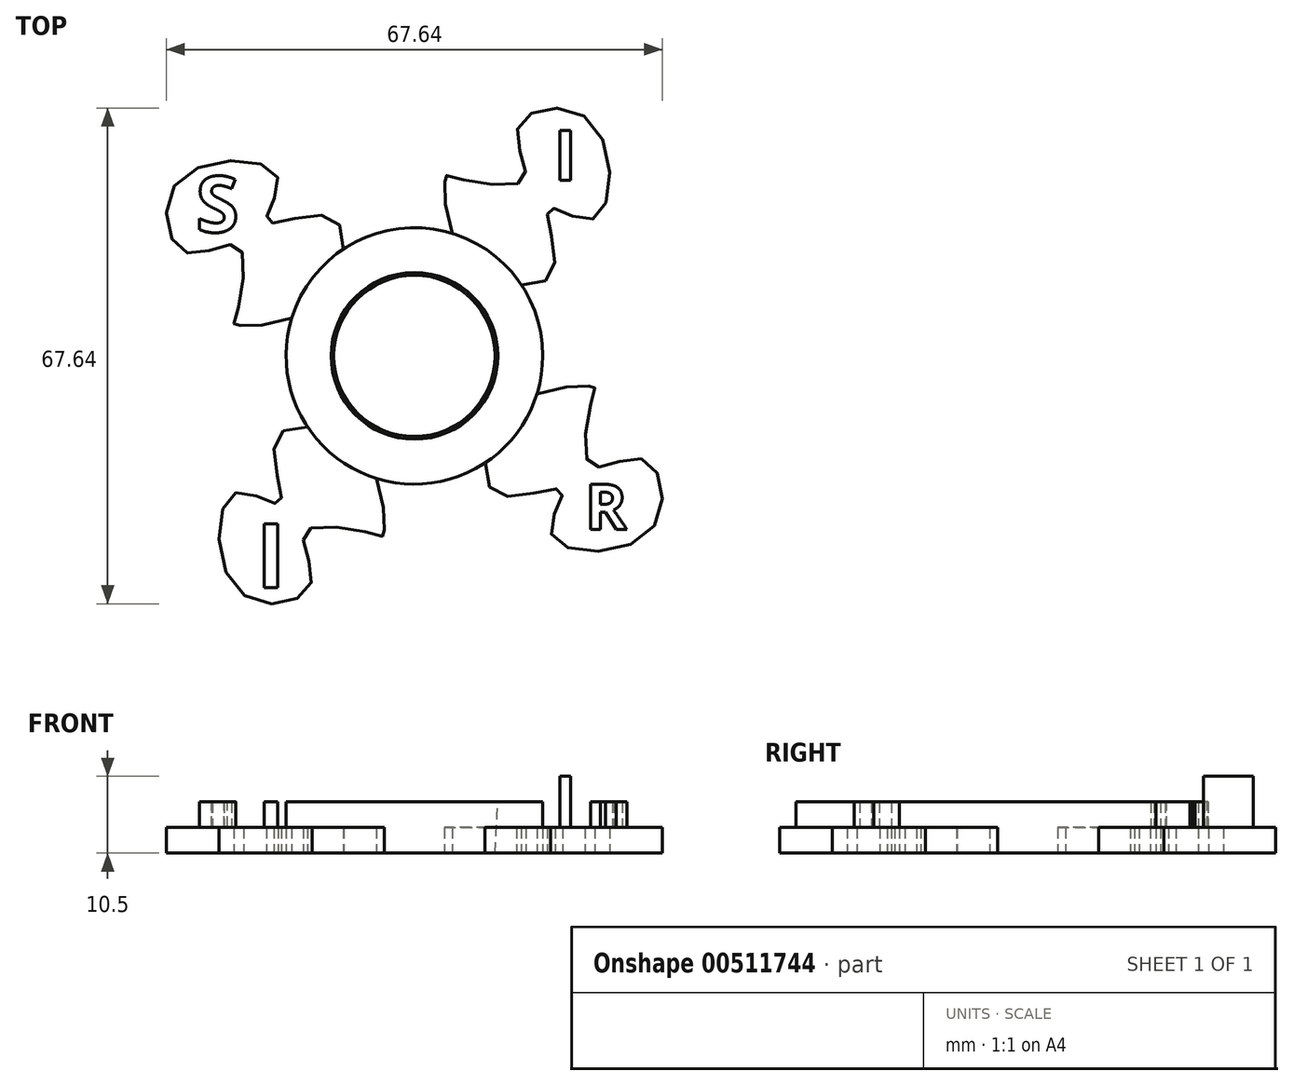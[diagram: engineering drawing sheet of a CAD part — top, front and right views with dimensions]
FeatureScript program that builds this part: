
annotation { "Feature Type Name" : "Feature", "Feature Type Description" : "" }
export const myFeature = defineFeature(function(context is Context, id is Id, definition is map)
    precondition{}
    {
        {
            var Q0;
            Q0=qCreatedBy(makeId("Top.planeOp"),FACE);
            var sketch = newSketch(context, id + "F0", { "sketchPlane" : qUnion([Q0])});
            skCircle(sketch, "E0", {"center": v(0, 0) * mm, "radius": 17.5 * mm});
            skSolve(sketch);
        }
        {
            var Q0;
            Q0 = qSketchRegion(id + "F0", true);
            extrude(context, id + "F1", {"entities" : qUnion([Q0]), "depth" : 7 * mm});
        }
        {
            var Q0;
            Q0=qCreatedBy(makeId("Top.planeOp"),FACE);
            var sketch = newSketch(context, id + "F2", { "sketchPlane" : qUnion([Q0])});
            skCircle(sketch, "E1", {"center": v(0, 0) * mm, "radius": 11 * mm});
            skSolve(sketch);
        }
        {
            var Q0;
            Q0=makeQuery(id+"F2.imprint","IMPRINT",FACE,{"disambiguationData":[TD([[makeQuery(id+"F2.imprint","IMPRINT",EDGE,{"derivedFrom":sQuery(id+"F2.wireOp",EDGE,"E1")}),1.0]])]});
            extrude(context, id + "F3", {"entities" : qUnion([Q0]), "operationType" : NewBodyOperationType.REMOVE, "depth" : 25 * mm, "hasDraft" : true, "draftAngle" : 3 * degree});
        }
        {
            var Q0;
            Q0=qCreatedBy(makeId("Top.planeOp"),FACE);
            var sketch = newSketch(context, id + "F4", { "sketchPlane" : qUnion([Q0])});
            skFitSpline(sketch, "E2", {"points": [v(6.82, 13.77) * mm, v(4.24, 24.57) * mm, v(4.47, 24.57) * mm, v(14.8, 23.86) * mm, v(14.1, 31.14) * mm, v(23.96, 32.08) * mm, v(24.43, 18.7) * mm, v(18.33, 20.1) * mm, v(18.8, 11.18) * mm, v(6.82, 13.77) * mm]});
            skSolve(sketch);
        }
        {
            var Q0;
            Q0=makeQuery(id+"F4.imprint","IMPRINT",FACE,{"disambiguationData":[TD([[makeQuery(id+"F4.imprint","IMPRINT",EDGE,{"derivedFrom":sQuery(id+"F4.wireOp",EDGE,"E2")}),-1.0]])]});
            extrude(context, id + "F5", {"entities" : qUnion([Q0]), "operationType" : NewBodyOperationType.ADD, "depth" : 7 / 2 * mm});
        }
        {
            var Q0;
            Q0=makeQuery(id+"F1.opExtrude","SWEPT_BODY",BODY,{"disambiguationData":[OSD([sQuery(id+"F0.wireOp",EDGE,"E0")])]});
            var Q1;
            Q1=makeQuery(id+"F1.opExtrude","CAP_EDGE",EDGE,{"disambiguationData":[OSD([sQuery(id+"F0.wireOp",EDGE,"E0")])],"isStart":false});
            circularPattern(context, id + "F6", {"operationType" : NewBodyOperationType.ADD, "entities" : qUnion([Q0]), "axis" : qUnion([Q1]), "angle" : 360 * degree, "instanceCount" : 4, "equalSpace" : true});
        }
        {
            var Q0;
            Q0=makeQuery(id+"F6.opPattern","COPY",FACE,{"derivedFrom":makeQuery(id+"F5.opExtrude","CAP_FACE",FACE,{"disambiguationData":[OSD([sQuery(id+"F4.wireOp",EDGE,"E2")])],"isStart":false}),"instanceName":"1"});
            var sketch = newSketch(context, id + "F7", { "sketchPlane" : qUnion([Q0])});
            skText(sketch, "E3", { "text": "I", "fontName": "OpenSans-Bold.ttf"});
            const initialGuessF7  = {"E3": [0.01901, 0.02398, 1, 0, 0.00681]};
            skSetInitialGuess(sketch, initialGuessF7);
            skSolve(sketch);
        }
        {
            var Q0;
            Q0=makeQuery(id+"F7.imprint","IMPRINT",FACE,{"disambiguationData":[TD([[makeQuery(id+"F7.imprint","IMPRINT",EDGE,{"derivedFrom":sQuery(id+"F7.wireOp",EDGE,"E3.sketch_text.stroke-0")}),-1.0]])]});
            extrude(context, id + "F8", {"entities" : qUnion([Q0]), "operationType" : NewBodyOperationType.ADD, "depth" : 7 * mm});
        }
        {
            var Q0;
            Q0=qCreatedBy(makeId("Top.planeOp"),FACE);
            var sketch = newSketch(context, id + "F9", { "sketchPlane" : qUnion([Q0])});
            skText(sketch, "E4", { "text": "R", "fontName": "OpenSans-Bold.ttf"});
            const initialGuessF9  = {"E4": [0.02327, -0.0237, 1, 0, 0.00624]};
            skSetInitialGuess(sketch, initialGuessF9);
            skSolve(sketch);
        }
        {
            var Q0;
            Q0=makeQuery(id+"F9.imprint","IMPRINT",FACE,{"disambiguationData":[TD([[makeQuery(id+"F9.imprint","IMPRINT",EDGE,{"derivedFrom":sQuery(id+"F9.wireOp",EDGE,"E4.sketch_text.stroke-0")}),-1.0]])]});
            extrude(context, id + "F10", {"entities" : qUnion([Q0]), "operationType" : NewBodyOperationType.ADD, "depth" : 7 * mm});
        }
        {
            var Q0;
            Q0=qCreatedBy(makeId("Top.planeOp"),FACE);
            var sketch = newSketch(context, id + "F11", { "sketchPlane" : qUnion([Q0])});
            skText(sketch, "E5", { "text": "I", "fontName": "OpenSans-Bold.ttf"});
            const initialGuessF11  = {"E5": [-0.02157, -0.03164, 1, 0, 0.0088]};
            skSetInitialGuess(sketch, initialGuessF11);
            skSolve(sketch);
        }
        {
            var Q0;
            Q0 = qSketchRegion(id + "F11", true);
            extrude(context, id + "F12", {"entities" : qUnion([Q0]), "operationType" : NewBodyOperationType.ADD, "depth" : 7 * mm});
        }
        {
            var Q0;
            Q0=qCreatedBy(makeId("Top.planeOp"),FACE);
            var sketch = newSketch(context, id + "F13", { "sketchPlane" : qUnion([Q0])});
            skText(sketch, "E6", { "text": "S", "fontName": "OpenSans-Bold.ttf"});
            const initialGuessF13  = {"E6": [-0.0298, 0.01689, 1, 0, 0.00766]};
            skSetInitialGuess(sketch, initialGuessF13);
            skSolve(sketch);
        }
        {
            var Q0;
            Q0 = qSketchRegion(id + "F13", true);
            extrude(context, id + "F14", {"entities" : qUnion([Q0]), "operationType" : NewBodyOperationType.ADD, "depth" : 7 * mm});
        }
    });
